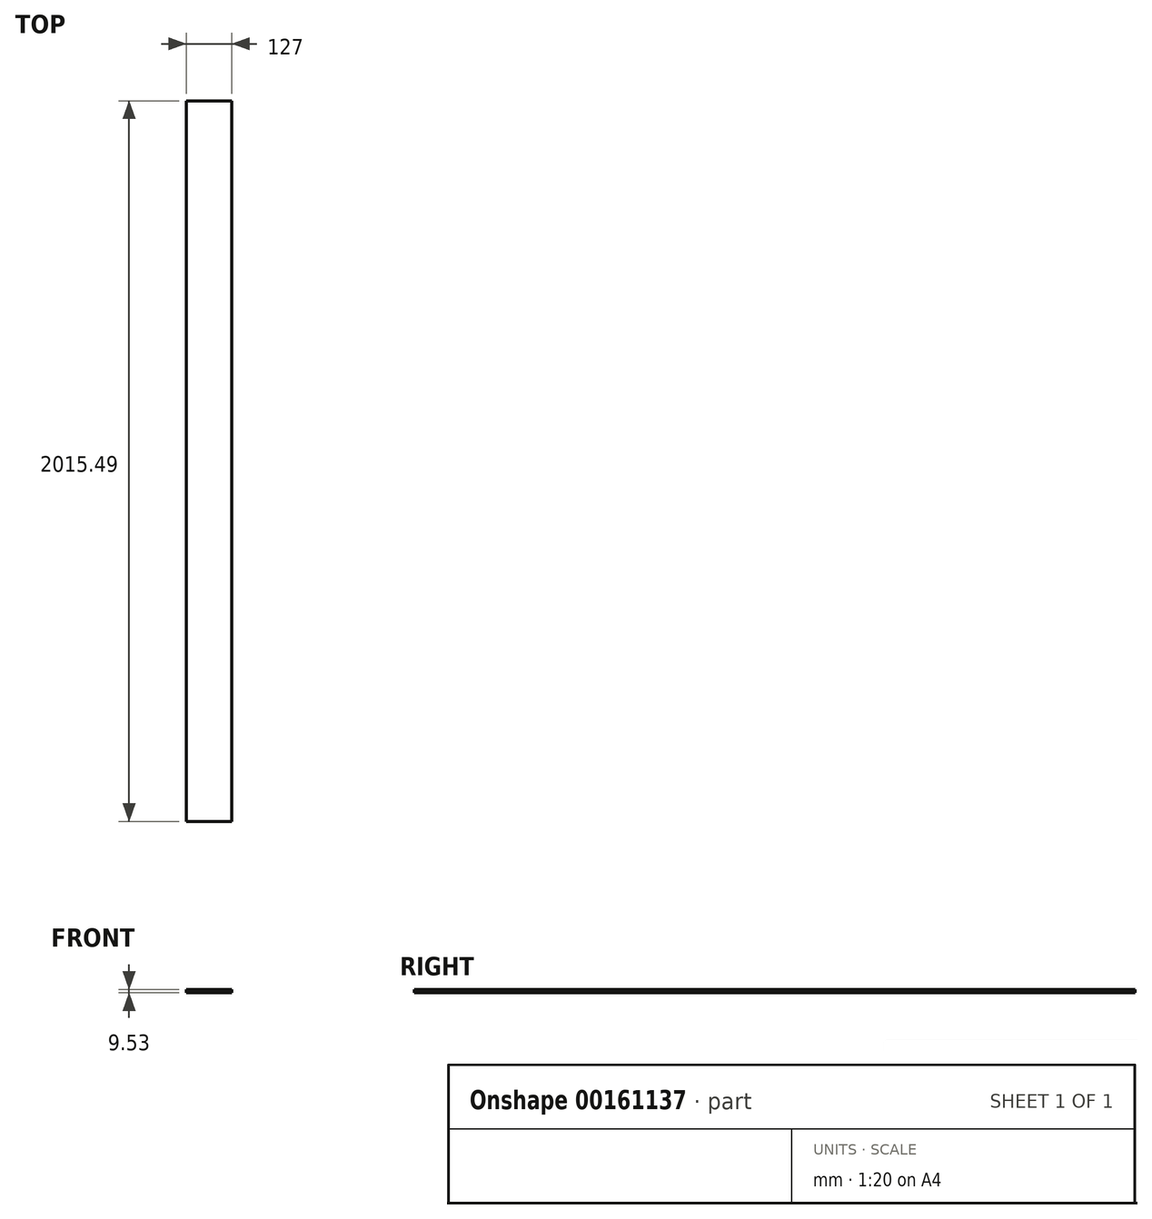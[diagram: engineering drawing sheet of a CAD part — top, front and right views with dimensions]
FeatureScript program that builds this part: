
annotation { "Feature Type Name" : "Feature", "Feature Type Description" : "" }
export const myFeature = defineFeature(function(context is Context, id is Id, definition is map)
    precondition{}
    {
        {
            var Q0;
            Q0=qCreatedBy(makeId("Front.planeOp"),FACE);
            var sketch = newSketch(context, id + "F0", { "sketchPlane" : qUnion([Q0])});
            skLineSegment(sketch, "E0.bottom", {"start": v(0, 0) * mm, "end": v(127, 0) * mm});
            skLineSegment(sketch, "E0.top", {"start": v(0, 9.53) * mm, "end": v(127, 9.53) * mm});
            skLineSegment(sketch, "E0.left", {"start": v(0, 0) * mm, "end": v(0, 9.53) * mm});
            skLineSegment(sketch, "E0.right", {"start": v(127, 0) * mm, "end": v(127, 9.53) * mm});
            skSolve(sketch);
        }
        {
            var Q0;
            Q0=qSketchRegion(id+"F0",true);
            extrude(context, id + "F1", {"entities" : qUnion([Q0]), "depth" : 2015.5 * mm});
        }
    });
